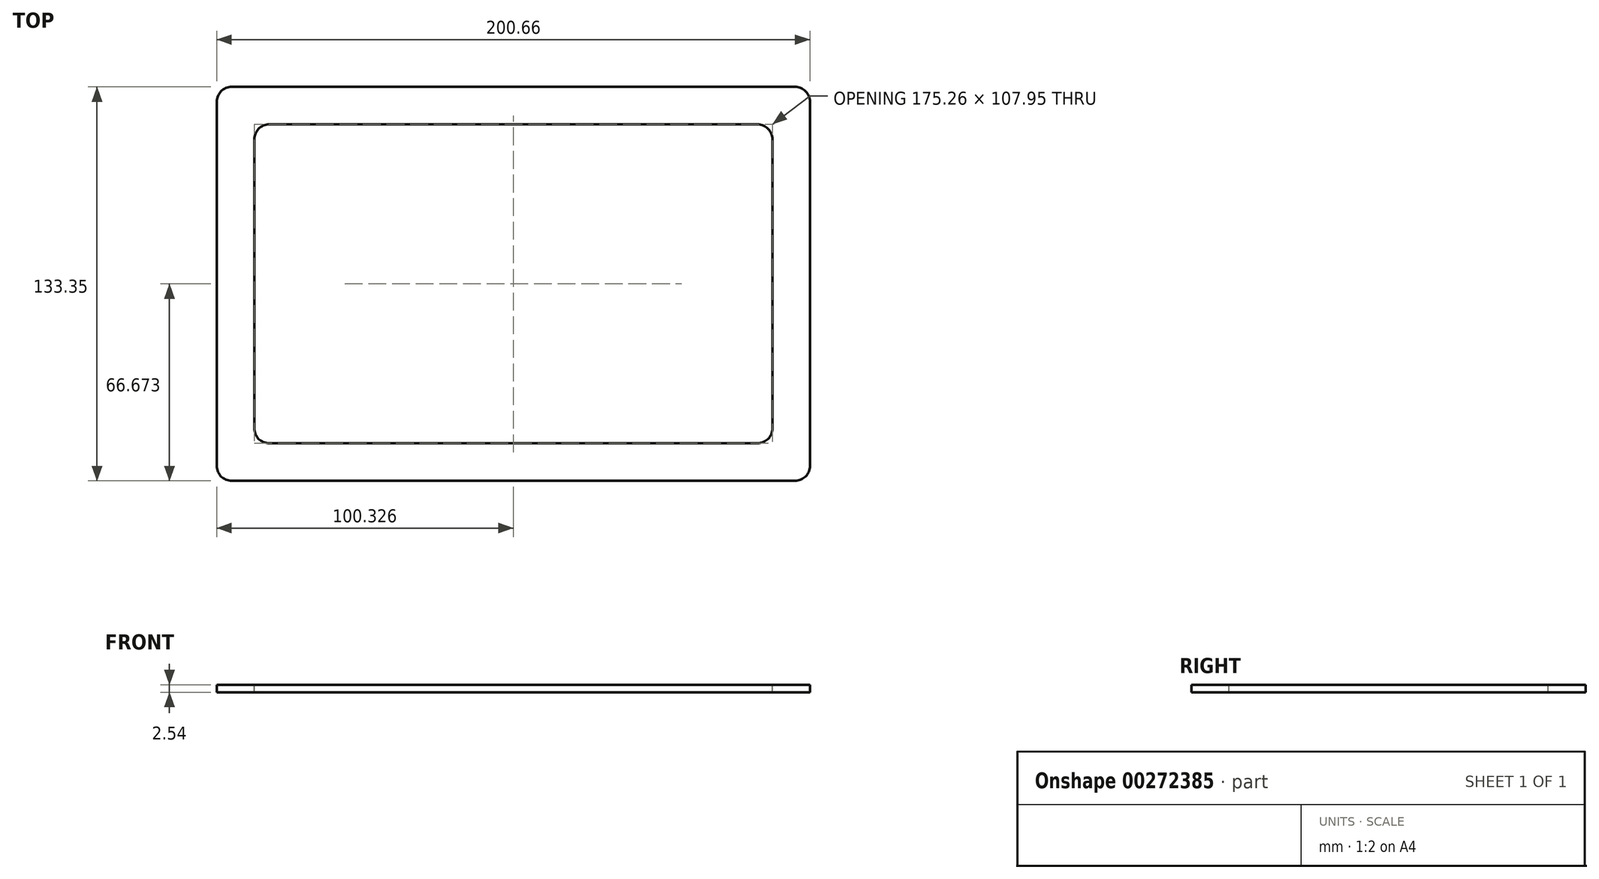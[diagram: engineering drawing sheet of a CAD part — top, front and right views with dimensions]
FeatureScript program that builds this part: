
annotation { "Feature Type Name" : "Feature", "Feature Type Description" : "" }
export const myFeature = defineFeature(function(context is Context, id is Id, definition is map)
    precondition{}
    {
        {
            var Q0;
            Q0=qCreatedBy(makeId("Top.planeOp"),FACE);
            var sketch = newSketch(context, id + "F0", { "sketchPlane" : qUnion([Q0])});
            skLineSegment(sketch, "E0.bottom", {"start": v(-131.02, 68.37) * mm, "end": v(69.64, 68.37) * mm});
            skLineSegment(sketch, "E0.top", {"start": v(-131.02, -64.98) * mm, "end": v(69.64, -64.98) * mm});
            skLineSegment(sketch, "E0.left", {"start": v(-131.02, 68.37) * mm, "end": v(-131.02, -64.98) * mm});
            skLineSegment(sketch, "E0.right", {"start": v(69.64, 68.37) * mm, "end": v(69.64, -64.98) * mm});
            skSolve(sketch);
        }
        {
            var Q0;
            Q0 = qSketchRegion(id + "F0", true);
            extrude(context, id + "F1", {"entities" : qUnion([Q0]), "depth" : 2.54 * mm});
        }
        {
            var Q0;
            Q0=makeQuery(id+"F1.opExtrude","SWEPT_EDGE",EDGE,{"disambiguationData":[OSD([sQuery(id+"F0.wireOp",EDGE,"E0.top"),sQuery(id+"F0.wireOp",EDGE,"E0.right")])]});
            var Q1;
            Q1=makeQuery(id+"F1.opExtrude","SWEPT_EDGE",EDGE,{"disambiguationData":[OSD([sQuery(id+"F0.wireOp",EDGE,"E0.bottom"),sQuery(id+"F0.wireOp",EDGE,"E0.right")])]});
            var Q2;
            Q2=makeQuery(id+"F1.opExtrude","SWEPT_EDGE",EDGE,{"disambiguationData":[OSD([sQuery(id+"F0.wireOp",EDGE,"E0.top"),sQuery(id+"F0.wireOp",EDGE,"E0.left")])]});
            var Q3;
            Q3=makeQuery(id+"F1.opExtrude","SWEPT_EDGE",EDGE,{"disambiguationData":[OSD([sQuery(id+"F0.wireOp",EDGE,"E0.bottom"),sQuery(id+"F0.wireOp",EDGE,"E0.left")])]});
            fillet(context, id + "F2", {"entities" : qUnion([Q0, Q1, Q2, Q3]), "radius" : 5.08 * mm, "tangentPropagation" : true, "allowEdgeOverflow" : false});
        }
        {
            var Q0;
            Q0=makeQuery(id+"F1.opExtrude","CAP_FACE",FACE,{"disambiguationData":[OSD([sQuery(id+"F0.wireOp",EDGE,"E0.bottom"),sQuery(id+"F0.wireOp",EDGE,"E0.top"),sQuery(id+"F0.wireOp",EDGE,"E0.left"),sQuery(id+"F0.wireOp",EDGE,"E0.right")])],"isStart":false});
            var sketch = newSketch(context, id + "F3", { "sketchPlane" : qUnion([Q0])});
            skLineSegment(sketch, "E1.0", {"start": v(-118.32, 55.67) * mm, "end": v(-118.32, -52.28) * mm});
            skLineSegment(sketch, "E1.1", {"start": v(56.94, 55.67) * mm, "end": v(-118.32, 55.67) * mm});
            skLineSegment(sketch, "E1.2", {"start": v(56.94, -52.28) * mm, "end": v(56.94, 55.67) * mm});
            skLineSegment(sketch, "E1.3", {"start": v(-118.32, -52.28) * mm, "end": v(56.94, -52.28) * mm});
            skSolve(sketch);
        }
        {
            var Q0;
            Q0=makeQuery(id+"F3.imprint","IMPRINT",FACE,{"disambiguationData":[TD([[makeQuery(id+"F3.imprint","IMPRINT",EDGE,{"derivedFrom":sQuery(id+"F3.wireOp",EDGE,"E1.0")}),1.0]])]});
            extrude(context, id + "F4", {"entities" : qUnion([Q0]), "operationType" : NewBodyOperationType.REMOVE, "oppositeDirection" : true, "depth" : 5.08 * mm});
        }
        {
            var Q0;
            Q0=makeQuery(id+"F4.boolean.opBoolean","COPY",EDGE,{"derivedFrom":makeQuery(id+"F4.opExtrude","SWEPT_EDGE",EDGE,{"disambiguationData":[OSD([sQuery(id+"F3.wireOp",EDGE,"E1.0"),sQuery(id+"F3.wireOp",EDGE,"E1.3")])]})});
            var Q1;
            Q1=makeQuery(id+"F4.boolean.opBoolean","COPY",EDGE,{"derivedFrom":makeQuery(id+"F4.opExtrude","SWEPT_EDGE",EDGE,{"disambiguationData":[OSD([sQuery(id+"F3.wireOp",EDGE,"E1.2"),sQuery(id+"F3.wireOp",EDGE,"E1.3")])]})});
            var Q2;
            Q2=makeQuery(id+"F4.boolean.opBoolean","COPY",EDGE,{"derivedFrom":makeQuery(id+"F4.opExtrude","SWEPT_EDGE",EDGE,{"disambiguationData":[OSD([sQuery(id+"F3.wireOp",EDGE,"E1.1"),sQuery(id+"F3.wireOp",EDGE,"E1.2")])]})});
            var Q3;
            Q3=makeQuery(id+"F4.boolean.opBoolean","COPY",EDGE,{"derivedFrom":makeQuery(id+"F4.opExtrude","SWEPT_EDGE",EDGE,{"disambiguationData":[OSD([sQuery(id+"F3.wireOp",EDGE,"E1.0"),sQuery(id+"F3.wireOp",EDGE,"E1.1")])]})});
            fillet(context, id + "F5", {"entities" : qUnion([Q0, Q1, Q2, Q3]), "radius" : 5.08 * mm, "tangentPropagation" : true, "allowEdgeOverflow" : false});
        }
    });
